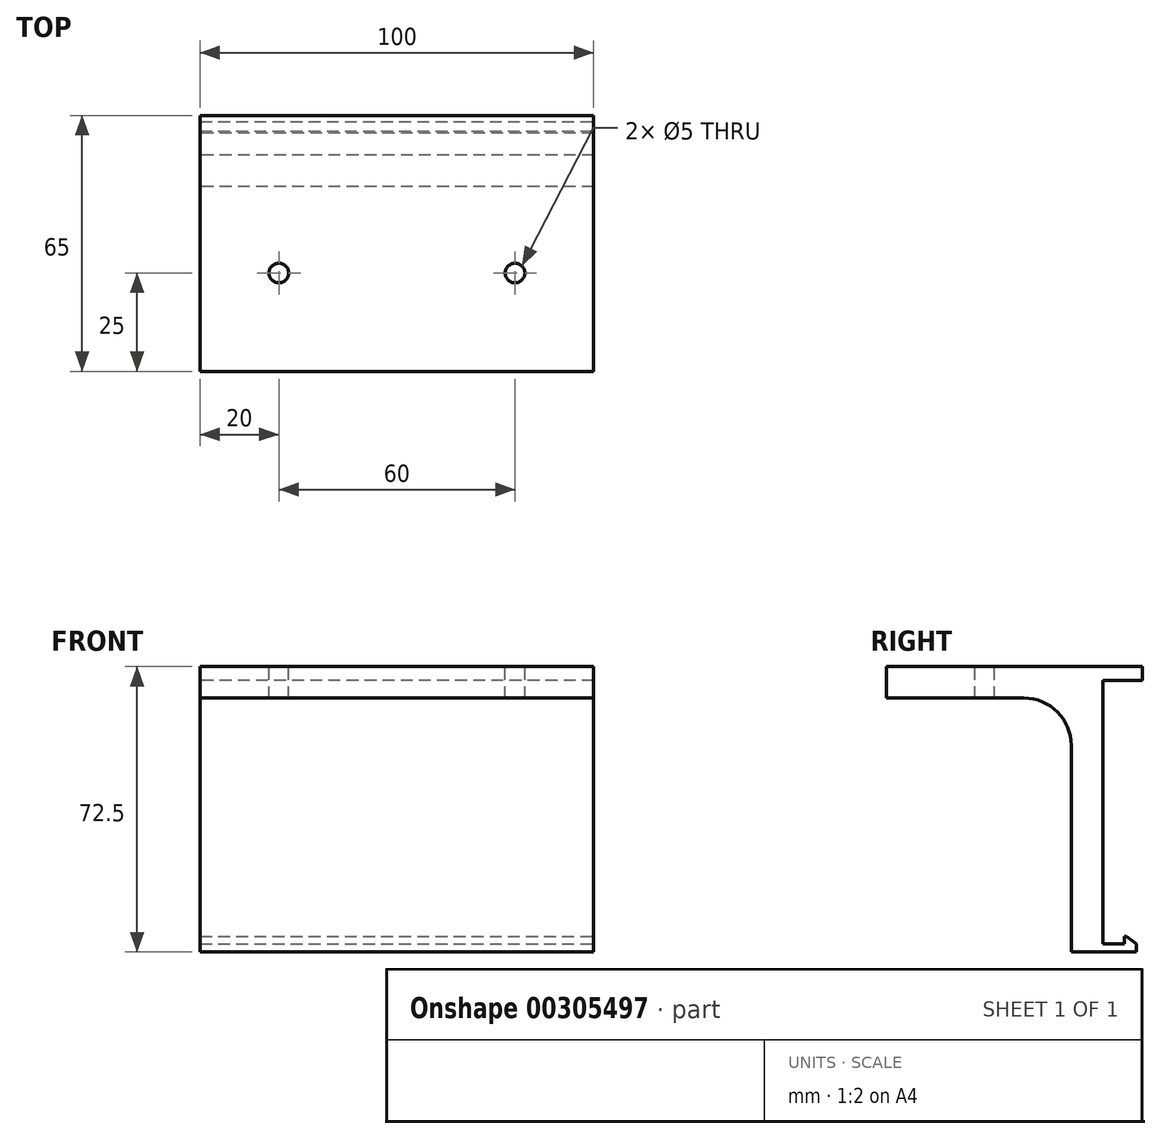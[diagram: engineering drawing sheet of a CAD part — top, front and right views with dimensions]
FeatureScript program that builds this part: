
annotation { "Feature Type Name" : "Feature", "Feature Type Description" : "" }
export const myFeature = defineFeature(function(context is Context, id is Id, definition is map)
    precondition{}
    {
        {
            var Q0;
            Q0=qCreatedBy(makeId("Right.planeOp"),FACE);
            var sketch = newSketch(context, id + "F0", { "sketchPlane" : qUnion([Q0])});
            skLineSegment(sketch, "E0", {"start": v(0, 0) * mm, "end": v(-65, 0) * mm});
            skLineSegment(sketch, "E1", {"start": v(-65, 0) * mm, "end": v(-65, -8) * mm});
            skLineSegment(sketch, "E2", {"start": v(0, 0) * mm, "end": v(0, -3.5) * mm});
            skLineSegment(sketch, "E3", {"start": v(0, -3.5) * mm, "end": v(-10, -3.5) * mm});
            skLineSegment(sketch, "E4", {"start": v(-10, -3.5) * mm, "end": v(-10, -70.5) * mm});
            skLineSegment(sketch, "E5", {"start": v(-10, -70.5) * mm, "end": v(-4.5, -70.5) * mm});
            skLineSegment(sketch, "E6", {"start": v(-4.5, -70.5) * mm, "end": v(-4.5, -68.5) * mm});
            skLineSegment(sketch, "E7", {"start": v(-4.5, -68.5) * mm, "end": v(-1.5, -68.5) * mm});
            skLineSegment(sketch, "E8", {"start": v(-1.5, -68.5) * mm, "end": v(-1.5, -72.5) * mm});
            skLineSegment(sketch, "E9", {"start": v(-1.5, -72.5) * mm, "end": v(-18, -72.5) * mm});
            skLineSegment(sketch, "E10", {"start": v(-18, -72.5) * mm, "end": v(-18, -8) * mm});
            skLineSegment(sketch, "E11", {"start": v(-65, -8) * mm, "end": v(-18, -8) * mm});
            skSolve(sketch);
        }
        {
            var Q0;
            Q0=makeQuery(id+"F0.imprint","IMPRINT",FACE,{"disambiguationData":[TD([[makeQuery(id+"F0.imprint","IMPRINT",EDGE,{"derivedFrom":sQuery(id+"F0.wireOp",EDGE,"E0")}),1.0]])]});
            extrude(context, id + "F1", {"entities" : qUnion([Q0]), "endBound" : BoundingType.SYMMETRIC, "depth" : 100 * mm});
        }
        {
            var Q0;
            Q0=makeQuery(id+"F1.opExtrude","CAP_FACE",FACE,{"disambiguationData":[OSD([sQuery(id+"F0.wireOp",EDGE,"E0"),sQuery(id+"F0.wireOp",EDGE,"E1"),sQuery(id+"F0.wireOp",EDGE,"E2"),sQuery(id+"F0.wireOp",EDGE,"E3"),sQuery(id+"F0.wireOp",EDGE,"E4"),sQuery(id+"F0.wireOp",EDGE,"E5"),sQuery(id+"F0.wireOp",EDGE,"E6"),sQuery(id+"F0.wireOp",EDGE,"E7"),sQuery(id+"F0.wireOp",EDGE,"E8"),sQuery(id+"F0.wireOp",EDGE,"E9"),sQuery(id+"F0.wireOp",EDGE,"E10"),sQuery(id+"F0.wireOp",EDGE,"E11")])],"isStart":false});
            var sketch = newSketch(context, id + "F2", { "sketchPlane" : qUnion([Q0])});
            skLineSegment(sketch, "E12", {"start": v(-4.5, -68.5) * mm, "end": v(-4, -68.5) * mm, "construction": true});
            skPoint(sketch, "E12.endSnap0", {"position": v(-3, -68.5) * mm});
            skLineSegment(sketch, "E13", {"start": v(-4, -68.5) * mm, "end": v(-1.5, -70.5) * mm});
            skLineSegment(sketch, "E14", {"start": v(-1.5, -70.5) * mm, "end": v(-1.5, -68.5) * mm});
            skLineSegment(sketch, "E15", {"start": v(-1.5, -68.5) * mm, "end": v(-4, -68.5) * mm});
            skSolve(sketch);
        }
        {
            var Q0;
            Q0=makeQuery(id+"F2.imprint","IMPRINT",FACE,{"disambiguationData":[TD([[makeQuery(id+"F2.imprint","IMPRINT",EDGE,{"derivedFrom":sQuery(id+"F2.wireOp",EDGE,"E13")}),1.0]])]});
            extrude(context, id + "F3", {"entities" : qUnion([Q0]), "operationType" : NewBodyOperationType.REMOVE, "endBound" : BoundingType.UP_TO_NEXT, "oppositeDirection" : true, "depth" : 25 * mm});
        }
        {
            var Q0;
            Q0=makeQuery(id+"F1.opExtrude","SWEPT_FACE",FACE,{"disambiguationData":[OSD([sQuery(id+"F0.wireOp",EDGE,"E0")])]});
            var sketch = newSketch(context, id + "F4", { "sketchPlane" : qUnion([Q0])});
            skLineSegment(sketch, "E16", {"start": v(-50, -65) * mm, "end": v(-50, -40) * mm, "construction": true});
            skLineSegment(sketch, "E17", {"start": v(-50, -40) * mm, "end": v(-30, -40) * mm, "construction": true});
            skLineSegment(sketch, "E18", {"start": v(-30, -40) * mm, "end": v(30, -40) * mm, "construction": true});
            skCircle(sketch, "E19", {"center": v(-30, -40) * mm, "radius": 2.5 * mm});
            skCircle(sketch, "E20", {"center": v(30, -40) * mm, "radius": 2.5 * mm});
            skSolve(sketch);
        }
        {
            var Q0;
            Q0=makeQuery(id+"F4.imprint","IMPRINT",FACE,{"disambiguationData":[TD([[makeQuery(id+"F4.imprint","IMPRINT",EDGE,{"derivedFrom":sQuery(id+"F4.wireOp",EDGE,"E19")}),1.0]])]});
            var Q1;
            Q1=makeQuery(id+"F4.imprint","IMPRINT",FACE,{"disambiguationData":[TD([[makeQuery(id+"F4.imprint","IMPRINT",EDGE,{"derivedFrom":sQuery(id+"F4.wireOp",EDGE,"E20")}),1.0]])]});
            extrude(context, id + "F5", {"entities" : qUnion([Q0, Q1]), "operationType" : NewBodyOperationType.REMOVE, "endBound" : BoundingType.UP_TO_NEXT, "oppositeDirection" : true, "depth" : 25 * mm});
        }
        {
            var Q0;
            Q0=makeQuery(id+"F1.opExtrude","SWEPT_EDGE",EDGE,{"disambiguationData":[OSD([sQuery(id+"F0.wireOp",EDGE,"E10"),sQuery(id+"F0.wireOp",EDGE,"E11")])]});
            fillet(context, id + "F6", {"entities" : qUnion([Q0]), "radius" : 12 * mm, "tangentPropagation" : true, "allowEdgeOverflow" : false});
        }
    });
